# Revit family: Double Skin Roofing_Roofwhite (STC 36_Uvalue 0.45)
name_source: partatom
category: Generic Models
units: mm (PartAtom-declared; Revit-internal decimal feet)

## family parameters
Can host rebar = No
Cut with Voids When Loaded = No
Host = Face
Part Type = Normal
Room Calculation Point = No
Round Connector Dimension = Use Diameter
Shared = No

## types (1)
- ROOFWHITE EWBL 2.00
    A = 76.5 mm  [stored 0.250984 ft]
    Actual Width (mm) = 3000 mm  [stored 9.84252 ft]
    Aluminium foil = Prelaminated Foil
    ArrayNum = 3
    ArrayNum (Top Skin) = 9
    Default Elevation = 0 mm  [stored 0 ft]
    Description = ECOWOOL Brownie blanket and slabs are resilient, non-combustible, glass mineral wool products, supplied at roofing and walling application for residential and commercial building
    Finish = Steel, High Grade
    Insulation = ROOFWHITE
    Insulation Density = 16 kg/m³
    Insulation Density (kg/m3) = 16 mm  [stored 0.0524934 ft]
    Insulation thk. (mm) = 75 mm
    Length (mm) = 2000 mm  [stored 6.56168 ft]
    Length Insulation = 2000 mm  [stored 6.56168 ft]
    Manufacturer = PGF Insulation Sdn. Bhd.
    ProVisSingle (Top Skin) = No
    ProfArrN = 3
    ProfArrN (Top Skin) = 9
    ProfVisDouble = Yes
    ProfVisDouble (Top Skin) = Yes
    ProfVisSingle = No
    Remarks = Double skin metal roof for Shop Office, Indoor Sport. Commonly used in government buildings- classroom, admin blocks, canteen, workshop, multipurpose hall, stores.
    STC = STC 36
    STC in dB = 36
    Spacer = Steel, High Grade
    SubL = 2805 mm  [stored 9.20276 ft]
    SubL (Top Skin) = 2718 mm  [stored 8.91732 ft]
    SubW = 3740 mm
    SubW (Top Skin) = 3020 mm  [stored 9.90814 ft]
    System Description = 1. Metal Deck Underliner
2. Ecowool  Roofwhite (c/w Foil)
3. 50mm Z spacer
4. Metal Deck
    Thermal K Value = 0.0366
    Thermal R Value = 2
    Total System Thickness-mm = 0 mm  [stored 0 ft]
    Type of Insulation = Blanket with vapour barrier
    Typical weight of ECOWOOL-Kg/M2 = 0 mm  [stored 0 ft]
    U Value = 0.45
    URL = www.ecowool.com.my
    Z Spacer No = 4

note: [stored X ft] marks values corroborated as IEEE doubles in the binary element streams (Revit-internal decimal feet)

## geometry (parser evidence)
native form markers: Sweep x27
no freeform markers — native parametric forms only
